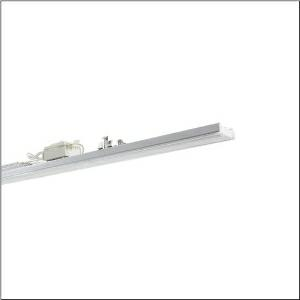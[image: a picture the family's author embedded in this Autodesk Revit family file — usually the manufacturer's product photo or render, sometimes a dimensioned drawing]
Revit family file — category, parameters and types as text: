
# Revit family: licross_r__11_recessed_extreme_mo_51te18dv4e5ge_323a
name_source: partatom
category: Lighting Fixtures
units: mm (PartAtom-declared; Revit-internal decimal feet)

## family parameters
Cut with Voids When Loaded = No
Host = Face
Light Source = No
Part Type = Normal
Room Calculation Point = No
Round Connector Dimension = Use Diameter
Shared = No

## types (1)
- --- (1 x LED, 14980 lm, 84.5 W, 4000K)
    Apparent Load = 85 VA
    CIE Flux Codes = 83 96 99 100 100
    Color Rendering = 80
    Color Temperature = 4000K
    Default Elevation = 1800 mm
    Description = Licross® 11 Recessed extreme MO, luminaire insert, of sheet steel, galvanised, coil coated, white, length: 2.250mm, width: 66mm, height: 67mm, LED rated luminous flux: 14.980lm, light colour: 840, control gear: DALI 2, with plug, 5-pole, with phase selection, mains connection: 220..240V, AC, 50/60Hz, rated input power: 85W, internal wiring halogen-free, primary light control with lens, of plastic, primary optical cover: cover, of PMMA, light emission: direct distribution, primary light characteristic: symmetric, protection rating (complete): IP54, insulation class (complete): insulation class I (protective earthing), certification: CE, ENEC, VDE, UKCA, protection symbol: D if used in an environment with non-conductive dust loads with corresponding accessories, impact resistance: IK06, permissible ambient temperature for indoor applications: -25..+45°C, corresponds to IFS (International Featured Standards) requirements for safety and quality in the food industry, reducing of maximum allowable ambient temperature of 5°C with ceiling mounting, LABS conformity tested according to VDMA 24364:2018-05, packaging unit: 1 piece
    Height = 58 mm
    Lamp = 1 x LED
    Lamp Light Flux = 14980 lm
    Lamp Power = 84.5 W
    Lamp count = 1
    Length = 2250 mm
    Luminous efficacy = 177 lm/W
    Manufacturer = Siteco
    ModVariant = No
    Model = 51TE18DV4E5GE
    Mounting Place = Ceiling
    Mounting Type = Pendant
    Number of Poles = 1
    OnlyDefault = Yes
    Power Factor = 1
    Product Name = Licross® 11 Recessed extreme MO
    Product group = luminaire insert | ceiling pendant
    ProductGroupID = 902
    Protection Class = Protection class I
    Protection Degree = IP 54
    RLX_Detail_Level = 1
    RLX_Emergency_Light_Flux = 0 lm
    RLX_Emergency_Type = 0
    RLX_Emergency_Type_DB = No
    RlxData = <blob elided: 29621 chars, md5=d051d01f>
    Socket = socket
    Standby Power = 0 W
    System Light Flux = 14980 lm
    System Power = 85 W
    Type Comments = factory setting: luminous flux: 100 % | dim-lin: 254 | 380 mA
    Type Image = l_1296930.jpg
    URL = http://relux.com
    VarID = @adj_111291
    Voltage = 0 V
    Weight = 0.00 kg
    Width = 66 mm

## geometry (parser evidence)
native form markers: Blend x4, Sweep x8
no freeform markers — native parametric forms only
